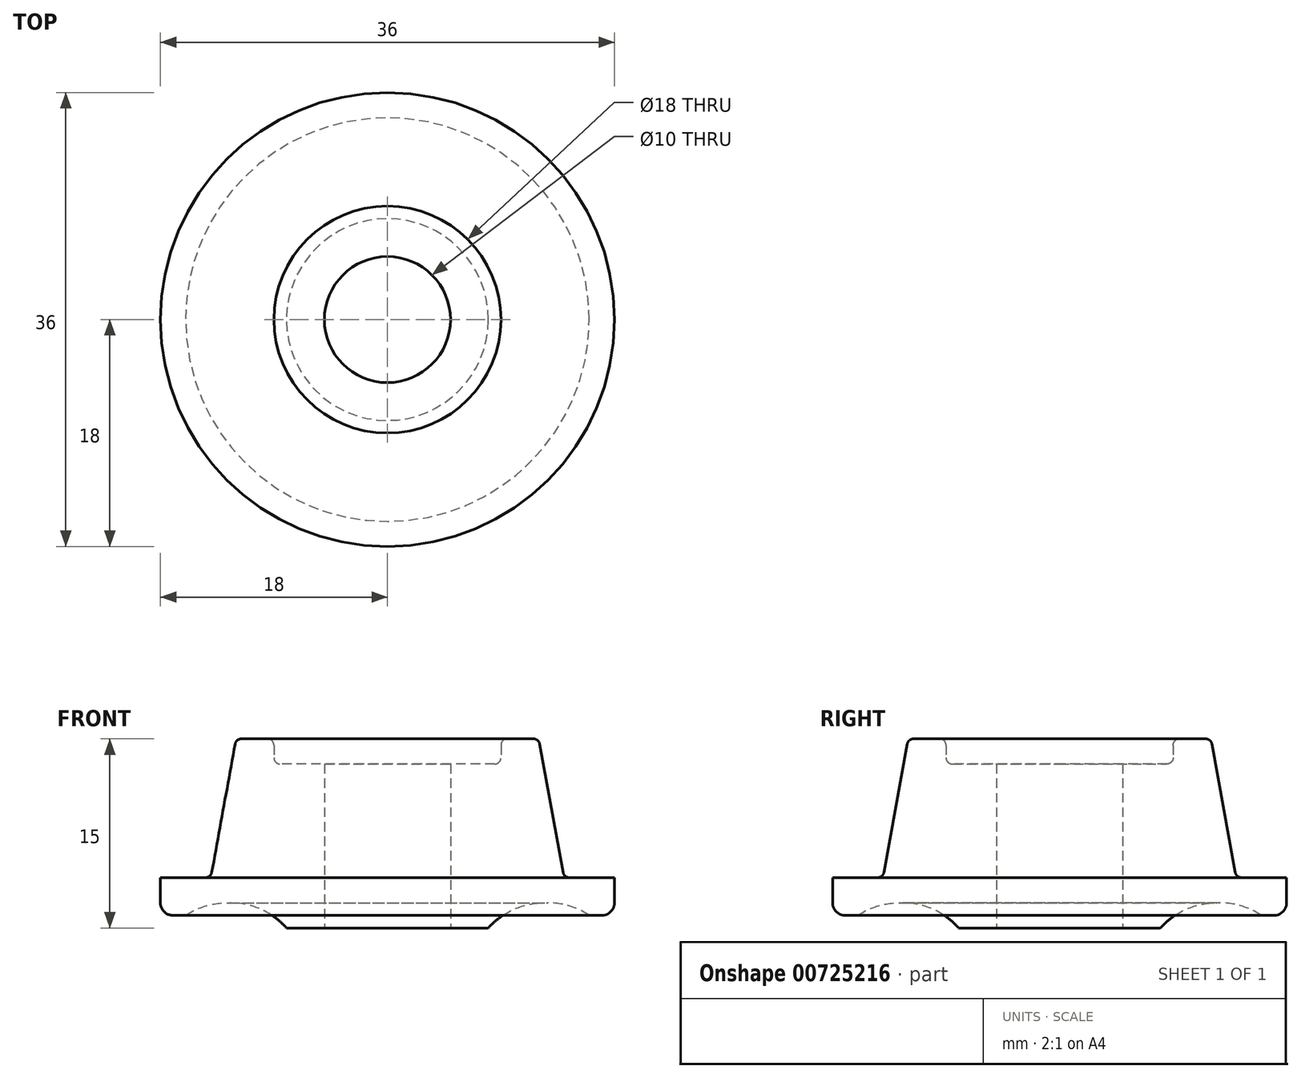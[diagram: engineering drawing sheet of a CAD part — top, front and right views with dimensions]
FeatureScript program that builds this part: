
annotation { "Feature Type Name" : "Feature", "Feature Type Description" : "" }
export const myFeature = defineFeature(function(context is Context, id is Id, definition is map)
    precondition{}
    {
        {
            var Q0;
            Q0=qCreatedBy(makeId("Right.planeOp"),FACE);
            var sketch = newSketch(context, id + "F0", { "sketchPlane" : qUnion([Q0])});
            skLineSegment(sketch, "E0", {"start": v(18, 0) * mm, "end": v(18, 3) * mm});
            skLineSegment(sketch, "E1", {"start": v(18, 3) * mm, "end": v(14, 3) * mm});
            skLineSegment(sketch, "E2", {"start": v(14, 3) * mm, "end": v(12, 14) * mm});
            skLineSegment(sketch, "E3", {"start": v(12, 14) * mm, "end": v(9, 14) * mm});
            skLineSegment(sketch, "E4", {"start": v(9, 14) * mm, "end": v(9, 12) * mm});
            skLineSegment(sketch, "E5", {"start": v(9, 12) * mm, "end": v(5, 12) * mm});
            skLineSegment(sketch, "E6", {"start": v(5, 12) * mm, "end": v(5, 0) * mm});
            skLineSegment(sketch, "E7", {"start": v(0, 0) * mm, "end": v(0, 33.74) * mm, "construction": true});
            skLineSegment(sketch, "E8", {"start": v(8, 0) * mm, "end": v(8, 1) * mm});
            skLineSegment(sketch, "E9", {"start": v(5, 0) * mm, "end": v(8, 0) * mm});
            skLineSegment(sketch, "E10", {"start": v(16, 1) * mm, "end": v(16, 0) * mm});
            skLineSegment(sketch, "E11", {"start": v(16, 0) * mm, "end": v(18, 0) * mm});
            skLineSegment(sketch, "E12", {"start": v(8, 1) * mm, "end": v(16, 1) * mm});
            skLineSegment(sketch, "E13", {"start": v(5, 0) * mm, "end": v(5, -1) * mm});
            skLineSegment(sketch, "E14", {"start": v(5, -1) * mm, "end": v(8, -1) * mm});
            skLineSegment(sketch, "E15", {"start": v(8, -1) * mm, "end": v(8, 0) * mm});
            skSolve(sketch);
        }
        {
            var Q0;
            Q0=makeQuery(id+"F0.imprint","IMPRINT",FACE,{"disambiguationData":[TD([[makeQuery(id+"F0.imprint","IMPRINT",EDGE,{"derivedFrom":sQuery(id+"F0.wireOp",EDGE,"E0")}),1.0]])]});
            var Q1;
            Q1=makeQuery(id+"F0.imprint","IMPRINT",FACE,{"disambiguationData":[TD([[makeQuery(id+"F0.imprint","IMPRINT",EDGE,{"derivedFrom":sQuery(id+"F0.wireOp",EDGE,"E9")}),-1.0]])]});
            var Q2;
            Q2=sQuery(id+"F0.wireOp",EDGE,"E7");
            revolve(context, id + "F1", {"surfaceOperationType" : NewSurfaceOperationType.NEW, "entities" : qUnion([Q0, Q1]), "axis" : qUnion([Q2]), "revolveType" : RevolveType.FULL});
        }
        {
            var Q0;
            Q0=makeQuery(id+"F1.opRevolve","SWEPT_EDGE",EDGE,{"disambiguationData":[OSD([sQuery(id+"F0.wireOp",EDGE,"E0"),sQuery(id+"F0.wireOp",EDGE,"E11")])]});
            fillet(context, id + "F2", {"entities" : qUnion([Q0]), "radius" : 1 * mm, "tangentPropagation" : true, "allowEdgeOverflow" : false});
        }
        {
            var Q0;
            Q0=makeQuery(id+"F1.opRevolve","SWEPT_EDGE",EDGE,{"disambiguationData":[OSD([sQuery(id+"F0.wireOp",EDGE,"E2"),sQuery(id+"F0.wireOp",EDGE,"E3")])]});
            var Q1;
            Q1=makeQuery(id+"F1.opRevolve","SWEPT_EDGE",EDGE,{"disambiguationData":[OSD([sQuery(id+"F0.wireOp",EDGE,"E1"),sQuery(id+"F0.wireOp",EDGE,"E2")])]});
            var Q2;
            Q2=makeQuery(id+"F1.opRevolve","SWEPT_EDGE",EDGE,{"disambiguationData":[OSD([sQuery(id+"F0.wireOp",EDGE,"E4"),sQuery(id+"F0.wireOp",EDGE,"E5")])]});
            var Q3;
            Q3=makeQuery(id+"F1.opRevolve","SWEPT_EDGE",EDGE,{"disambiguationData":[OSD([sQuery(id+"F0.wireOp",EDGE,"E3"),sQuery(id+"F0.wireOp",EDGE,"E4")])]});
            fillet(context, id + "F3", {"entities" : qUnion([Q0, Q1, Q2, Q3]), "radius" : 0.5 * mm, "tangentPropagation" : true, "allowEdgeOverflow" : false});
        }
        {
            var Q0;
            Q0=makeQuery(id+"F1.opRevolve","SWEPT_EDGE",EDGE,{"disambiguationData":[OSD([sQuery(id+"F0.wireOp",EDGE,"E8"),sQuery(id+"F0.wireOp",EDGE,"E12")])]});
            var Q1;
            Q1=makeQuery(id+"F1.opRevolve","SWEPT_EDGE",EDGE,{"disambiguationData":[OSD([sQuery(id+"F0.wireOp",EDGE,"E10"),sQuery(id+"F0.wireOp",EDGE,"E12")])]});
            fillet(context, id + "F4", {"entities" : qUnion([Q0, Q1]), "radius" : 6 * mm, "tangentPropagation" : true, "allowEdgeOverflow" : false});
        }
    });
